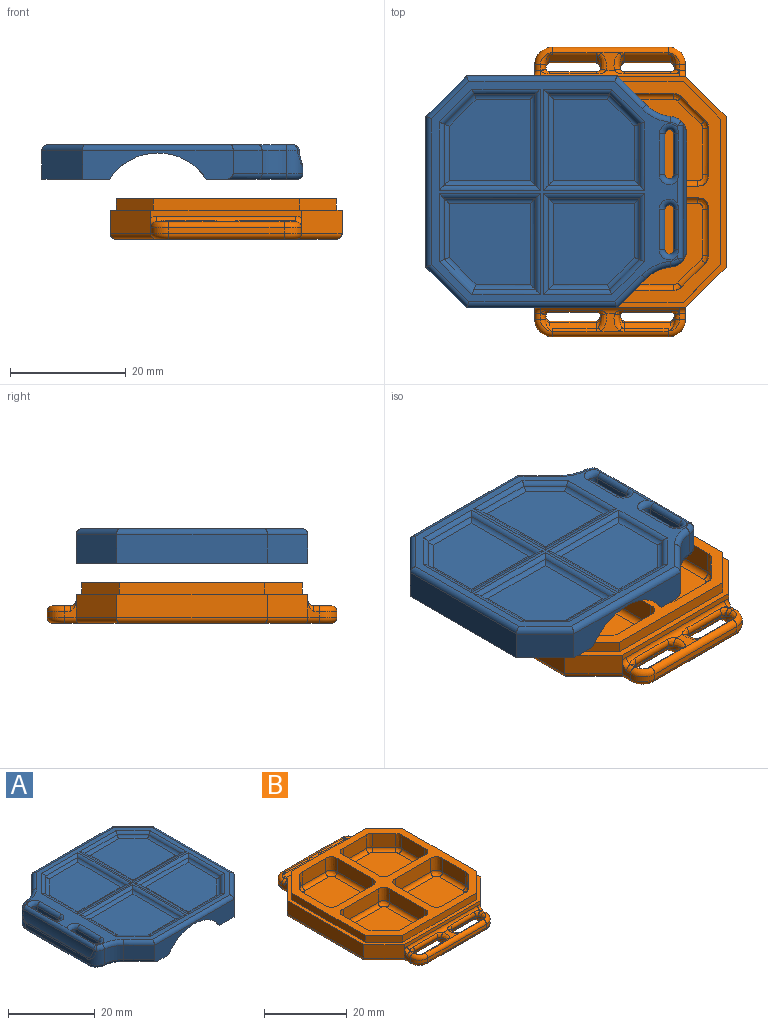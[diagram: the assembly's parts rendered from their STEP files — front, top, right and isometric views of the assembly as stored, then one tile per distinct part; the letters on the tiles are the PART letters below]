
ASSEMBLY  parts=2 mates=1
PART A: 123 faces, bbox 45.2x41.4x6 mm
  f0: plane 4.18x1mm, normal (0,0,-1), area 3.7mm2, adj f4,f22,f62,f69
  f1: plane 4.18x1mm, normal (0,0,-1), area 3.7mm2, adj f12,f17,f62,f63
  f2: plane 28.6x6.71mm, normal (0,0,-1), area 52.9mm2, adj f13,f14,f15,f64,f65,f66,f67,f68
  f3: plane 7.2x3mm, normal (0,1,0), area 16.4mm2, adj f6,f7,f11,f62
  f4: plane 26x5mm, normal (0,1,0), area 75.5mm2, adj f0,f7,f20,f21,f62,f69,f82
  f5: plane 7.2x3mm, normal (0,-1,0), area 16.4mm2, adj f6,f7,f9,f62
  f6: plane 38x13.61mm, normal (0,0,-1), area 476.1mm2, adj f3,f5,f9,f10,f11,f62
  f7: plane 40x11.6mm, normal (0,0,-1), area 53.3mm2, adj f3,f4,f5,f9,f10,f11,f17,f18
  f8: plane 42.38x38mm, normal (0,0,1), area 251.6mm2, adj f78,f79,f80,f81,f82,f83,f84,f85
  f9: plane 6.41x6.41mm, normal (-0.71,-0.71,0), area 27.2mm2, adj f5,f6,f7,f10
  f10: plane 25.17x3mm, normal (-1,0,0), area 75.5mm2, adj f6,f7,f9,f11
  f11: plane 6.41x6.41mm, normal (-0.71,0.71,0), area 27.2mm2, adj f3,f6,f7,f10
  f12: plane 7.2x3mm, normal (0,1,0), area 16.4mm2, adj f1,f13,f23,f62
  f13: plane 6.41x6.41mm, normal (0.71,0.71,0), area 27.2mm2, adj f2,f12,f14,f23,f63
  f14: plane 25.17x3mm, normal (1,0,0), area 75.5mm2, adj f2,f13,f15,f23
  f15: plane 6.41x6.41mm, normal (0.71,-0.71,0), area 27.2mm2, adj f2,f14,f22,f23,f69
  f16: plane 4.99x4.99mm, normal (-0.71,-0.71,0), area 28.3mm2, adj f17,f53,f63,f83
  f17: plane 26x5mm, normal (0,-1,0), area 75.5mm2, adj f1,f7,f16,f18,f62,f63,f81
  f18: plane 7x7mm, normal (0.71,-0.71,0), area 49.5mm2, adj f7,f17,f19,f79
  f19: plane 26x5mm, normal (1,0,0), area 130mm2, adj f7,f18,f20,f78
  f20: plane 7x7mm, normal (0.71,0.71,0), area 49.5mm2, adj f4,f7,f19,f80
  f21: plane 4.99x4.99mm, normal (-0.71,0.71,0), area 28.3mm2, adj f4,f52,f69,f84
  f22: plane 7.2x3mm, normal (0,-1,0), area 16.4mm2, adj f0,f15,f23,f62
  f23: plane 38x13.61mm, normal (0,0,-1), area 476.1mm2, adj f12,f13,f14,f15,f22,f62
  f24: plane 14x14mm, normal (0,0,1), area 185.2mm2, adj f43,f44,f45,f46,f47
  f25: plane 14x14mm, normal (0,0,1), area 185.2mm2, adj f38,f39,f40,f41,f42
  f26: plane 14x14mm, normal (0,0,1), area 185.2mm2, adj f28,f29,f30,f31,f32
  f27: plane 14x14mm, normal (0,0,1), area 185.2mm2, adj f33,f34,f35,f36,f37
  f28: cylinder r=1mm len=15.73mm, axis (0,-1,0), area 15.6mm2, adj f26,f29,f30,f122
  f29: cylinder r=1mm len=10.57mm, axis (-1,0,0), area 10.4mm2, adj f26,f28,f31,f121
  f30: cylinder r=1mm len=15.73mm, axis (1,0,0), area 15.6mm2, adj f26,f28,f32,f120
  f31: cylinder r=1mm len=5.78mm, axis (-0.71,0.71,0), area 7.3mm2, adj f26,f29,f32,f119
  f32: cylinder r=1mm len=10.57mm, axis (0,1,0), area 10.4mm2, adj f26,f30,f31,f118
  f33: cylinder r=1mm len=10.57mm, axis (0,-1,0), area 10.4mm2, adj f27,f34,f35,f114
  f34: cylinder r=1mm len=5.78mm, axis (-0.71,-0.71,0), area 7.3mm2, adj f27,f33,f36,f116
  f35: cylinder r=1mm len=15.73mm, axis (1,0,0), area 15.6mm2, adj f27,f33,f37,f113
  f36: cylinder r=1mm len=10.57mm, axis (-1,0,0), area 10.4mm2, adj f27,f34,f37,f117
  f37: cylinder r=1mm len=15.73mm, axis (0,1,0), area 15.6mm2, adj f27,f35,f36,f115
  f38: cylinder r=1mm len=5.78mm, axis (0.71,-0.71,0), area 7.3mm2, adj f25,f39,f40,f111
  f39: cylinder r=1mm len=10.57mm, axis (0,-1,0), area 10.4mm2, adj f25,f38,f41,f109
  f40: cylinder r=1mm len=10.57mm, axis (1,0,0), area 10.4mm2, adj f25,f38,f42,f112
  f41: cylinder r=1mm len=15.73mm, axis (-1,0,0), area 15.6mm2, adj f25,f39,f42,f108
  f42: cylinder r=1mm len=15.73mm, axis (0,1,0), area 15.6mm2, adj f25,f40,f41,f110
  f43: cylinder r=1mm len=15.73mm, axis (0,-1,0), area 15.6mm2, adj f24,f44,f45,f106
  f44: cylinder r=1mm len=15.73mm, axis (-1,0,0), area 15.6mm2, adj f24,f43,f46,f104
  f45: cylinder r=1mm len=10.57mm, axis (1,0,0), area 10.4mm2, adj f24,f43,f47,f107
  f46: cylinder r=1mm len=10.57mm, axis (0,1,0), area 10.4mm2, adj f24,f44,f47,f103
  f47: cylinder r=1mm len=5.78mm, axis (0.71,0.71,0), area 7.3mm2, adj f24,f45,f46,f105
  f48: plane 20x1.26mm, normal (-1,0,0), area 25.1mm2, adj f49,f50,f66,f86
  f49: cylinder r=3mm len=4mm, axis (0,0,1), area 12.8mm2, adj f48,f52,f67,f90,f91
  f50: cylinder r=3mm len=4mm, axis (0,0,-1), area 12.8mm2, adj f48,f53,f65,f88,f89
  f51: cylinder r=10mm len=22.9mm, axis (0,1,0), area 56.9mm2, adj f86,f89,f90,f100
  f52: cylinder r=7mm len=4.29mm, axis (0,0,1), area 19.3mm2, adj f21,f49,f68,f87
  f53: cylinder r=7mm len=4.29mm, axis (0,0,-1), area 19.3mm2, adj f16,f50,f64,f85
  f54: plane 7x4mm, normal (-1,0,0), area 28mm2, adj f55,f57,f70,f92
  f55: cylinder r=0.75mm len=4mm, axis (0,0,-1), area 9.4mm2, adj f54,f56,f72,f97
  f56: plane 7x4mm, normal (1,0,0), area 28mm2, adj f55,f57,f73,f96
  f57: cylinder r=0.75mm len=4mm, axis (0,0,-1), area 9.4mm2, adj f54,f56,f71,f95
  f58: cylinder r=0.75mm len=4mm, axis (0,0,-1), area 9.4mm2, adj f59,f61,f76,f102
  f59: plane 7x4mm, normal (-1,0,0), area 28mm2, adj f58,f60,f74,f101
  f60: cylinder r=0.75mm len=4mm, axis (0,0,-1), area 9.4mm2, adj f59,f61,f75,f98
  f61: plane 7x4mm, normal (1,0,0), area 28mm2, adj f58,f60,f77,f99
  f62: cylinder r=10mm len=40mm, axis (0,1,0), area 472.5mm2, adj f0,f1,f3,f4,f5,f6,f7,f12
  f63: cylinder r=1mm len=6.41mm, axis (-0.71,0.71,0), area 11.7mm2, adj f1,f13,f16,f17,f64
  f64: torus R=8mm, axis (0,0,1), area 8mm2, adj f2,f53,f63,f65
  f65: torus R=2mm, axis (0,0,1), area 6.1mm2, adj f2,f50,f64,f66
  f66: cylinder r=1mm len=20mm, axis (0,1,0), area 31.4mm2, adj f2,f48,f65,f67
  f67: torus R=2mm, axis (0,0,1), area 6.1mm2, adj f2,f49,f66,f68
  f68: torus R=8mm, axis (0,0,1), area 8mm2, adj f2,f52,f67,f69
  f69: cylinder r=1mm len=6.41mm, axis (0.71,0.71,0), area 11.7mm2, adj f0,f4,f15,f21,f68
  f70: cylinder r=1mm len=7mm, axis (0,-1,0), area 11mm2, adj f2,f54,f71,f72
  f71: torus R=1.75mm, axis (0,0,1), area 5.5mm2, adj f2,f57,f70,f73
  f72: torus R=1.75mm, axis (0,0,1), area 5.5mm2, adj f2,f55,f70,f73
  f73: cylinder r=1mm len=7mm, axis (0,1,0), area 11mm2, adj f2,f56,f71,f72
  f74: cylinder r=1mm len=7mm, axis (0,-1,0), area 11mm2, adj f2,f59,f75,f76
  f75: torus R=1.75mm, axis (0,0,1), area 5.5mm2, adj f2,f60,f74,f77
  f76: torus R=1.75mm, axis (0,0,1), area 5.5mm2, adj f2,f58,f74,f77
  f77: cylinder r=1mm len=7mm, axis (0,1,0), area 11mm2, adj f2,f61,f75,f76
  f78: cylinder r=1mm len=26mm, axis (0,1,0), area 40.2mm2, adj f8,f19,f79,f80
  f79: cylinder r=1mm len=7.71mm, axis (0.71,0.71,0), area 14.9mm2, adj f8,f18,f78,f81
  f80: cylinder r=1mm len=7.71mm, axis (-0.71,0.71,0), area 14.9mm2, adj f8,f20,f78,f82
  f81: cylinder r=1mm len=26mm, axis (1,0,0), area 40.2mm2, adj f8,f17,f79,f83
  f82: cylinder r=1mm len=26mm, axis (-1,0,0), area 40.2mm2, adj f4,f8,f80,f84
  f83: cylinder r=1mm len=5.7mm, axis (0.71,-0.71,0), area 10.8mm2, adj f8,f16,f81,f85
  f84: cylinder r=1mm len=5.7mm, axis (-0.71,-0.71,0), area 10.8mm2, adj f8,f21,f82,f87
  f85: torus R=8mm, axis (0,0,1), area 8mm2, adj f8,f53,f83,f88
  f86: cylinder r=1mm len=20mm, axis (0,1,0), area 7mm2, adj f48,f51,f89,f90
  f87: torus R=8mm, axis (0,0,1), area 8mm2, adj f8,f52,f84,f91
  f88: torus R=2mm, axis (0,0,1), area 2.8mm2, adj f8,f50,f85,f93
  f89: bspline ~3.06x2.45mm, area 2.1mm2, adj f50,f51,f86,f93
  f90: bspline ~3.06x2.45mm, area 2.1mm2, adj f49,f51,f86,f94
  f91: torus R=2mm, axis (0,0,1), area 2.8mm2, adj f8,f49,f87,f94
  f92: cylinder r=1mm len=7mm, axis (0,-1,0), area 11mm2, adj f8,f54,f95,f97
  f93: sphere r=1mm, area 0.8mm2, adj f88,f89,f100
  f94: sphere r=1mm, area 0.8mm2, adj f90,f91,f100
  f95: torus R=1.75mm, axis (0,0,1), area 5.4mm2, adj f8,f57,f92,f96,f100
  f96: cylinder r=1mm len=7mm, axis (0,1,0), area 9.7mm2, adj f56,f95,f97,f100
  f97: torus R=1.75mm, axis (0,0,1), area 5.4mm2, adj f8,f55,f92,f96,f100
  f98: torus R=1.75mm, axis (0,0,1), area 5.4mm2, adj f8,f60,f99,f100,f101
  f99: cylinder r=1mm len=7mm, axis (0,1,0), area 9.7mm2, adj f61,f98,f100,f102
  f100: cylinder r=1mm len=22.9mm, axis (0,1,0), area 30.8mm2, adj f8,f51,f93,f94,f95,f96,f97,f98
  f101: cylinder r=1mm len=7mm, axis (0,-1,0), area 11mm2, adj f8,f59,f98,f102
  f102: torus R=1.75mm, axis (0,0,1), area 5.4mm2, adj f8,f58,f99,f100,f101
  f103: cylinder r=1mm len=11.79mm, axis (0,1,0), area 11.7mm2, adj f8,f46,f104,f105
  f104: cylinder r=1mm len=17.46mm, axis (-1,0,0), area 17.4mm2, adj f8,f44,f103,f106
  f105: cylinder r=1mm len=6.28mm, axis (0.71,0.71,0), area 8mm2, adj f8,f47,f103,f107
  f106: cylinder r=1mm len=17.46mm, axis (0,-1,0), area 17.4mm2, adj f8,f43,f104,f107
  f107: cylinder r=1mm len=11.79mm, axis (1,0,0), area 11.7mm2, adj f8,f45,f105,f106
  f108: cylinder r=1mm len=17.46mm, axis (-1,0,0), area 17.4mm2, adj f8,f41,f109,f110
  f109: cylinder r=1mm len=11.79mm, axis (0,-1,0), area 11.7mm2, adj f8,f39,f108,f111
  f110: cylinder r=1mm len=17.46mm, axis (0,1,0), area 17.4mm2, adj f8,f42,f108,f112
  f111: cylinder r=1mm len=6.28mm, axis (0.71,-0.71,0), area 8mm2, adj f8,f38,f109,f112
  f112: cylinder r=1mm len=11.79mm, axis (1,0,0), area 11.7mm2, adj f8,f40,f110,f111
  f113: cylinder r=1mm len=17.46mm, axis (1,0,0), area 17.4mm2, adj f8,f35,f114,f115
  f114: cylinder r=1mm len=11.79mm, axis (0,-1,0), area 11.7mm2, adj f8,f33,f113,f116
  f115: cylinder r=1mm len=17.46mm, axis (0,1,0), area 17.4mm2, adj f8,f37,f113,f117
  f116: cylinder r=1mm len=6.28mm, axis (-0.71,-0.71,0), area 8mm2, adj f8,f34,f114,f117
  f117: cylinder r=1mm len=11.79mm, axis (-1,0,0), area 11.7mm2, adj f8,f36,f115,f116
  f118: cylinder r=1mm len=11.79mm, axis (0,1,0), area 11.7mm2, adj f8,f32,f119,f120
  f119: cylinder r=1mm len=6.28mm, axis (-0.71,0.71,0), area 8mm2, adj f8,f31,f118,f121
  f120: cylinder r=1mm len=17.46mm, axis (1,0,0), area 17.4mm2, adj f8,f30,f118,f122
  f121: cylinder r=1mm len=11.79mm, axis (-1,0,0), area 11.7mm2, adj f8,f29,f119,f122
  f122: cylinder r=1mm len=17.46mm, axis (0,-1,0), area 17.4mm2, adj f8,f28,f120,f121
PART B: 231 faces, bbox 40.2x50.7x7.6 mm
  f0: plane 9.05x0.34mm, normal (0,1,0), area 2.2mm2, adj f2,f193,f194,f196
  f1: plane 26x1.27mm, normal (0,1,0), area 26.2mm2, adj f38,f40,f44,f190,f191,f192
  f2: cylinder r=1mm len=10.39mm, axis (-1,0,0), area 15.2mm2, adj f0,f3,f194,f196,f202,f205
  f3: plane 48x38mm, normal (0,0,-1), area 1412.6mm2, adj f2,f112,f113,f114,f115,f116,f117,f118
  f4: plane 3.18x3mm, normal (0,0,1), area 5.2mm2, adj f127,f130,f153,f168
  f5: plane 38.21x38.21mm, normal (0,0,1), area 401.3mm2, adj f6,f7,f8,f9,f10,f12,f13,f14
  f6: plane 12x4mm, normal (-1,0,0), area 48mm2, adj f5,f50,f54,f75
  f7: plane 7.93x4mm, normal (0,-1,0), area 31.7mm2, adj f5,f54,f66,f71
  f8: plane 4.07x4.07mm, normal (0.71,-0.71,0), area 23mm2, adj f5,f65,f66,f67
  f9: plane 7.93x4mm, normal (1,0,0), area 31.7mm2, adj f5,f58,f65,f70
  f10: plane 12x4mm, normal (0,1,0), area 48mm2, adj f5,f50,f58,f74
  f11: plane 14x14mm, normal (0,0,1), area 184.8mm2, adj f67,f68,f69,f70,f71,f72,f73,f74
  f12: plane 7.93x4mm, normal (-1,0,0), area 31.7mm2, adj f5,f57,f62,f81
  f13: plane 4.07x4.07mm, normal (-0.71,-0.71,0), area 23mm2, adj f5,f62,f64,f77
  f14: plane 7.93x4mm, normal (0,-1,0), area 31.7mm2, adj f5,f53,f64,f80
  f15: plane 12x4mm, normal (1,0,0), area 48mm2, adj f5,f49,f53,f84
  f16: plane 12x4mm, normal (0,1,0), area 48mm2, adj f5,f49,f57,f85
  f17: plane 14x14mm, normal (0,0,1), area 184.8mm2, adj f77,f78,f79,f80,f81,f82,f83,f84
  f18: plane 12x4mm, normal (0,-1,0), area 48mm2, adj f5,f47,f55,f104
  f19: plane 12x4mm, normal (1,0,0), area 48mm2, adj f5,f47,f51,f105
  f20: plane 7.93x4mm, normal (0,1,0), area 31.7mm2, adj f5,f51,f60,f101
  f21: plane 4.07x4.07mm, normal (-0.71,0.71,0), area 23mm2, adj f5,f59,f60,f97
  f22: plane 7.93x4mm, normal (-1,0,0), area 31.7mm2, adj f5,f55,f59,f100
  f23: plane 14x14mm, normal (0,0,1), area 184.8mm2, adj f97,f98,f99,f100,f101,f102,f103,f104
  f24: plane 12x4mm, normal (-1,0,0), area 48mm2, adj f5,f48,f52,f94
  f25: plane 12x4mm, normal (0,-1,0), area 48mm2, adj f5,f48,f56,f95
  f26: plane 7.93x4mm, normal (1,0,0), area 31.7mm2, adj f5,f56,f63,f91
  f27: plane 4.07x4.07mm, normal (0.71,0.71,0), area 23mm2, adj f5,f61,f63,f87
  f28: plane 7.93x4mm, normal (0,1,0), area 31.7mm2, adj f5,f52,f61,f90
  f29: plane 14x14mm, normal (0,0,1), area 184.8mm2, adj f87,f88,f89,f90,f91,f92,f93,f94
  f30: plane 6.41x6.41mm, normal (0.71,0.71,0), area 18.1mm2, adj f5,f31,f37,f38
  f31: plane 25.17x2mm, normal (1,0,0), area 50.3mm2, adj f5,f30,f32,f38
  f32: plane 6.41x6.41mm, normal (0.71,-0.71,0), area 18.1mm2, adj f5,f31,f33,f38
  f33: plane 25.17x2mm, normal (0,-1,0), area 50.3mm2, adj f5,f32,f34,f38
  f34: plane 6.41x6.41mm, normal (-0.71,-0.71,0), area 18.1mm2, adj f5,f33,f35,f38
  f35: plane 25.17x2mm, normal (-1,0,0), area 50.3mm2, adj f5,f34,f36,f38
  f36: plane 6.41x6.41mm, normal (-0.71,0.71,0), area 18.1mm2, adj f5,f35,f37,f38
  f37: plane 25.17x2mm, normal (0,1,0), area 50.3mm2, adj f5,f30,f36,f38
  f38: plane 40x40mm, normal (0,0,1), area 140.3mm2, adj f1,f30,f31,f32,f33,f34,f35,f36
  f39: plane 7x7mm, normal (0.71,-0.71,0), area 39.6mm2, adj f38,f41,f43,f108,f115
  f40: plane 7x7mm, normal (0.71,0.71,0), area 39.6mm2, adj f1,f38,f41,f112,f176
  f41: plane 26x4mm, normal (1,0,0), area 104mm2, adj f38,f39,f40,f113
  f42: plane 7x7mm, normal (-0.71,-0.71,0), area 39.6mm2, adj f38,f43,f45,f107,f120
  f43: plane 26x1.27mm, normal (0,-1,0), area 26.2mm2, adj f38,f39,f42,f129,f130,f131
  f44: plane 7x7mm, normal (-0.71,0.71,0), area 39.6mm2, adj f1,f38,f45,f116,f175
  f45: plane 26x4mm, normal (-1,0,0), area 104mm2, adj f38,f42,f44,f118
  f46: plane 9.05x0.34mm, normal (0,1,0), area 2.2mm2, adj f114,f197,f199,f200
  f47: bspline ~5.5x2mm, area 13mm2, adj f5,f18,f19,f106
  f48: bspline ~5.5x2mm, area 13mm2, adj f5,f24,f25,f96
  f49: bspline ~5.5x2mm, area 13mm2, adj f5,f15,f16,f86
  f50: bspline ~5.5x2mm, area 13mm2, adj f5,f6,f10,f76
  f51: bspline ~5.5x2mm, area 13mm2, adj f5,f19,f20,f103
  f52: bspline ~5.5x2mm, area 13mm2, adj f5,f24,f28,f92
  f53: bspline ~5.5x2mm, area 13mm2, adj f5,f14,f15,f82
  f54: bspline ~5.5x2mm, area 13mm2, adj f5,f6,f7,f73
  f55: bspline ~5.5x2mm, area 13mm2, adj f5,f18,f22,f102
  f56: bspline ~5.5x2mm, area 13mm2, adj f5,f25,f26,f93
  f57: bspline ~5.5x2mm, area 13mm2, adj f5,f12,f16,f83
  f58: bspline ~5.5x2mm, area 13mm2, adj f5,f9,f10,f72
  f59: bspline ~5.5x1.41mm, area 6.3mm2, adj f5,f21,f22,f98
  f60: bspline ~5.5x1.41mm, area 6.3mm2, adj f5,f20,f21,f99
  f61: bspline ~5.5x1.41mm, area 6.3mm2, adj f5,f27,f28,f88
  f62: bspline ~5.5x1.41mm, area 6.3mm2, adj f5,f12,f13,f79
  f63: bspline ~5.5x1.41mm, area 6.3mm2, adj f5,f26,f27,f89
  f64: bspline ~5.5x1.41mm, area 6.3mm2, adj f5,f13,f14,f78
  f65: bspline ~5.5x1.41mm, area 6.3mm2, adj f5,f8,f9,f68
  f66: bspline ~5.5x1.41mm, area 6.3mm2, adj f5,f7,f8,f69
  f67: cylinder r=1mm len=4.78mm, axis (-0.71,-0.71,0), area 9mm2, adj f8,f11,f68,f69
  f68: bspline ~1.65x1.46mm, area 2mm2, adj f11,f65,f67,f70
  f69: bspline ~1.7x1.34mm, area 2mm2, adj f11,f66,f67,f71
  f70: cylinder r=1mm len=7.93mm, axis (0,-1,0), area 12.5mm2, adj f9,f11,f68,f72
  f71: cylinder r=1mm len=7.93mm, axis (-1,0,0), area 12.5mm2, adj f7,f11,f69,f73
  f72: bspline ~2.52x2.52mm, area 4.2mm2, adj f11,f58,f70,f74
  f73: bspline ~2.52x2.52mm, area 4.2mm2, adj f11,f54,f71,f75
  f74: cylinder r=1mm len=12mm, axis (1,0,0), area 18.8mm2, adj f10,f11,f72,f76
  f75: cylinder r=1mm len=12mm, axis (0,1,0), area 18.8mm2, adj f6,f11,f73,f76
  f76: bspline ~2.52x2.52mm, area 4.2mm2, adj f11,f50,f74,f75
  f77: cylinder r=1mm len=4.78mm, axis (-0.71,0.71,0), area 9mm2, adj f13,f17,f78,f79
  f78: bspline ~1.65x1.46mm, area 2mm2, adj f17,f64,f77,f80
  f79: bspline ~1.7x1.34mm, area 2mm2, adj f17,f62,f77,f81
  f80: cylinder r=1mm len=7.93mm, axis (-1,0,0), area 12.5mm2, adj f14,f17,f78,f82
  f81: cylinder r=1mm len=7.93mm, axis (0,1,0), area 12.5mm2, adj f12,f17,f79,f83
  f82: bspline ~2.52x2.52mm, area 4.2mm2, adj f17,f53,f80,f84
  f83: bspline ~2.52x2.52mm, area 4.2mm2, adj f17,f57,f81,f85
  f84: cylinder r=1mm len=12mm, axis (0,-1,0), area 18.8mm2, adj f15,f17,f82,f86
  f85: cylinder r=1mm len=12mm, axis (1,0,0), area 18.8mm2, adj f16,f17,f83,f86
  f86: bspline ~2.52x2.52mm, area 4.2mm2, adj f17,f49,f84,f85
  f87: cylinder r=1mm len=4.78mm, axis (0.71,-0.71,0), area 9mm2, adj f27,f29,f88,f89
  f88: bspline ~1.65x1.46mm, area 2mm2, adj f29,f61,f87,f90
  f89: bspline ~1.7x1.34mm, area 2mm2, adj f29,f63,f87,f91
  f90: cylinder r=1mm len=7.93mm, axis (1,0,0), area 12.5mm2, adj f28,f29,f88,f92
  f91: cylinder r=1mm len=7.93mm, axis (0,-1,0), area 12.5mm2, adj f26,f29,f89,f93
  f92: bspline ~2.52x2.52mm, area 4.2mm2, adj f29,f52,f90,f94
  f93: bspline ~2.52x2.52mm, area 4.2mm2, adj f29,f56,f91,f95
  f94: cylinder r=1mm len=12mm, axis (0,1,0), area 18.8mm2, adj f24,f29,f92,f96
  f95: cylinder r=1mm len=12mm, axis (-1,0,0), area 18.8mm2, adj f25,f29,f93,f96
  f96: bspline ~2.52x2.52mm, area 4.2mm2, adj f29,f48,f94,f95
  f97: cylinder r=1mm len=4.78mm, axis (0.71,0.71,0), area 9mm2, adj f21,f23,f98,f99
  f98: bspline ~1.65x1.46mm, area 2mm2, adj f23,f59,f97,f100
  f99: bspline ~1.7x1.34mm, area 2mm2, adj f23,f60,f97,f101
  f100: cylinder r=1mm len=7.93mm, axis (0,1,0), area 12.5mm2, adj f22,f23,f98,f102
  f101: cylinder r=1mm len=7.93mm, axis (1,0,0), area 12.5mm2, adj f20,f23,f99,f103
  f102: bspline ~2.52x2.52mm, area 4.2mm2, adj f23,f55,f100,f104
  f103: bspline ~2.52x2.52mm, area 4.2mm2, adj f23,f51,f101,f105
  f104: cylinder r=1mm len=12mm, axis (-1,0,0), area 18.8mm2, adj f18,f23,f102,f106
  f105: cylinder r=1mm len=12mm, axis (0,-1,0), area 18.8mm2, adj f19,f23,f103,f106
  f106: bspline ~2.52x2.52mm, area 4.2mm2, adj f23,f47,f104,f105
  f107: plane 2.73x2mm, normal (-1,0,0), area 2.6mm2, adj f42,f110,f122,f126,f131
  f108: plane 2.73x2mm, normal (1,0,0), area 2.6mm2, adj f39,f111,f117,f124,f129
  f109: plane 20x1mm, normal (0,-1,0), area 20mm2, adj f110,f111,f121,f127
  f110: cylinder r=3mm len=3mm, axis (0,0,1), area 4.7mm2, adj f107,f109,f123,f128
  f111: cylinder r=3mm len=3mm, axis (0,0,-1), area 4.7mm2, adj f108,f109,f119,f125
  f112: cylinder r=1mm len=8mm, axis (0.71,-0.71,0), area 15.6mm2, adj f3,f40,f113,f180
  f113: cylinder r=1mm len=26mm, axis (0,1,0), area 40.2mm2, adj f3,f41,f112,f115
  f114: cylinder r=1mm len=10.39mm, axis (-1,0,0), area 15.2mm2, adj f3,f46,f197,f199,f216,f217
  f115: cylinder r=1mm len=8mm, axis (0.71,0.71,0), area 15.6mm2, adj f3,f39,f113,f117
  f116: cylinder r=1mm len=8mm, axis (-0.71,-0.71,0), area 15.6mm2, adj f3,f44,f118,f183
  f117: cylinder r=1mm len=2.41mm, axis (0,1,0), area 3.4mm2, adj f3,f108,f115,f119,f140
  f118: cylinder r=1mm len=26mm, axis (0,-1,0), area 40.2mm2, adj f3,f45,f116,f120
  f119: torus R=2mm, axis (0,0,1), area 6.5mm2, adj f3,f111,f117,f121
  f120: cylinder r=1mm len=8mm, axis (-0.71,0.71,0), area 15.6mm2, adj f3,f42,f118,f122
  f121: cylinder r=1mm len=20mm, axis (-1,0,0), area 31.4mm2, adj f3,f109,f119,f123
  f122: cylinder r=1mm len=2.41mm, axis (0,1,0), area 3.4mm2, adj f3,f107,f120,f123,f158
  f123: torus R=2mm, axis (0,0,1), area 6.5mm2, adj f3,f110,f121,f122
  f124: cylinder r=1mm len=1mm, axis (0,-1,0), area 1.6mm2, adj f108,f125,f129,f146
  f125: torus R=2mm, axis (0,0,1), area 6.5mm2, adj f111,f124,f127,f145,f147
  f126: cylinder r=1mm len=1mm, axis (0,-1,0), area 1.6mm2, adj f107,f128,f131,f161
  f127: cylinder r=1mm len=20mm, axis (1,0,0), area 31.4mm2, adj f4,f109,f125,f128,f149,f151,f164,f166
  f128: torus R=2mm, axis (0,0,1), area 6.5mm2, adj f110,f126,f127,f160,f162
  f129: torus R=2mm, axis (0,1,0), area 1.9mm2, adj f43,f108,f124,f130,f148
  f130: cylinder r=1mm len=24mm, axis (1,0,0), area 24.7mm2, adj f4,f43,f129,f131,f150,f152,f154,f165
  f131: torus R=2mm, axis (0,1,0), area 1.9mm2, adj f43,f107,f126,f130,f163
  f132: plane 8x0.47mm, normal (0,-0.71,-0.71), area 5.3mm2, adj f133,f135,f152,f173
  f133: cylinder r=0.75mm len=3.97mm, axis (0,-0.71,0.71), area 2.8mm2, adj f132,f134,f144,f151,f153,f154,f172,f173
  f134: plane 8x1.09mm, normal (0,0.71,0.71), area 12mm2, adj f133,f135,f143,f147,f149
  f135: cylinder r=0.75mm len=4.01mm, axis (0,-0.71,0.71), area 3mm2, adj f132,f134,f140,f141,f142,f145,f146,f148
  f136: cylinder r=0.75mm len=4.01mm, axis (0,-0.71,0.71), area 3mm2, adj f137,f139,f156,f158,f159,f160,f161,f163
  f137: plane 8x1.09mm, normal (0,0.71,0.71), area 12mm2, adj f136,f138,f157,f162,f164
  f138: cylinder r=0.75mm len=3.97mm, axis (0,-0.71,0.71), area 2.8mm2, adj f137,f139,f155,f166,f168,f169,f170,f171
  f139: plane 8x0.47mm, normal (0,-0.71,-0.71), area 5.3mm2, adj f136,f138,f167,f171
  f140: bspline ~2.57x1.43mm, area 2.4mm2, adj f117,f135,f141,f142
  f141: bspline ~1.08x1.08mm, area 0.6mm2, adj f3,f135,f140,f172
  f142: bspline ~2.41x2.1mm, area 3mm2, adj f3,f135,f140,f143
  f143: cylinder r=1mm len=8mm, axis (1,0,0), area 18.8mm2, adj f3,f134,f142,f144
  f144: bspline ~4.5x2.2mm, area 6.2mm2, adj f3,f133,f143,f172
  f145: bspline ~2.02x1.66mm, area 1.9mm2, adj f125,f135,f146,f147
  f146: bspline ~1.58x1.28mm, area 1.3mm2, adj f124,f135,f145,f148
  f147: bspline ~0.64x0.36mm, area 0.2mm2, adj f125,f134,f145,f149
  f148: bspline ~1.29x0.94mm, area 0.2mm2, adj f129,f135,f146,f150
  f149: cylinder r=1mm len=7.59mm, axis (1,0,0), area 3.3mm2, adj f127,f134,f147,f151
  f150: bspline ~2.04x1.56mm, area 1.8mm2, adj f130,f135,f148,f152
  f151: bspline ~1.07x0.74mm, area 0.4mm2, adj f127,f133,f149,f153
  f152: cylinder r=1mm len=8mm, axis (1,0,0), area 13.5mm2, adj f130,f132,f150,f154
  f153: bspline ~3x1.4mm, area 3.5mm2, adj f4,f133,f151,f154
  f154: bspline ~2.06x1.56mm, area 2mm2, adj f130,f133,f152,f153
  f155: bspline ~4.5x2.2mm, area 6.2mm2, adj f3,f138,f157,f170
  f156: bspline ~1.08x1.08mm, area 0.6mm2, adj f3,f136,f158,f170
  f157: cylinder r=1mm len=8mm, axis (1,0,0), area 18.8mm2, adj f3,f137,f155,f159
  f158: bspline ~2.57x1.43mm, area 2.4mm2, adj f122,f136,f156,f159
  f159: bspline ~2.41x2.1mm, area 3mm2, adj f3,f136,f157,f158
  f160: bspline ~2.02x1.66mm, area 1.9mm2, adj f128,f136,f161,f162
  f161: bspline ~1.58x1.28mm, area 1.3mm2, adj f126,f136,f160,f163
  f162: bspline ~0.74x0.36mm, area 0.2mm2, adj f128,f137,f160,f164
  f163: bspline ~1.29x0.94mm, area 0.2mm2, adj f131,f136,f161,f165
  f164: cylinder r=1mm len=7.59mm, axis (1,0,0), area 3.3mm2, adj f127,f137,f162,f166
  f165: bspline ~2.04x1.56mm, area 1.8mm2, adj f130,f136,f163,f167
  f166: bspline ~1.07x0.74mm, area 0.4mm2, adj f127,f138,f164,f168
  f167: cylinder r=1mm len=8mm, axis (1,0,0), area 13.5mm2, adj f130,f139,f165,f169
  f168: bspline ~3x1.4mm, area 3.5mm2, adj f4,f138,f166,f169
  f169: bspline ~1.82x1.56mm, area 2mm2, adj f130,f138,f167,f168
  f170: cylinder r=1mm len=10.39mm, axis (-1,0,0), area 15.2mm2, adj f3,f136,f138,f155,f156,f171
  f171: plane 9.05x0.34mm, normal (0,-1,0), area 2.2mm2, adj f136,f138,f139,f170
  f172: cylinder r=1mm len=10.39mm, axis (-1,0,0), area 15.2mm2, adj f3,f133,f135,f141,f144,f173
  f173: plane 9.05x0.34mm, normal (0,-1,0), area 2.2mm2, adj f132,f133,f135,f172
  f174: plane 3.18x3mm, normal (0,0,1), area 5.2mm2, adj f188,f191,f214,f229
  f175: plane 2.73x2mm, normal (-1,0,0), area 2.6mm2, adj f44,f178,f183,f187,f192
  f176: plane 2.73x2mm, normal (1,0,0), area 2.6mm2, adj f40,f179,f180,f185,f190
  f177: plane 20x1mm, normal (0,1,0), area 20mm2, adj f178,f179,f182,f188
  f178: cylinder r=3mm len=3mm, axis (0,0,1), area 4.7mm2, adj f175,f177,f184,f189
  f179: cylinder r=3mm len=3mm, axis (0,0,-1), area 4.7mm2, adj f176,f177,f181,f186
  f180: cylinder r=1mm len=2.41mm, axis (0,-1,0), area 3.4mm2, adj f3,f112,f176,f181,f201
  f181: torus R=2mm, axis (0,0,1), area 6.5mm2, adj f3,f179,f180,f182
  f182: cylinder r=1mm len=20mm, axis (-1,0,0), area 31.4mm2, adj f3,f177,f181,f184
  f183: cylinder r=1mm len=2.41mm, axis (0,-1,0), area 3.4mm2, adj f3,f116,f175,f184,f219
  f184: torus R=2mm, axis (0,0,1), area 6.5mm2, adj f3,f178,f182,f183
  f185: cylinder r=1mm len=1mm, axis (0,1,0), area 1.6mm2, adj f176,f186,f190,f207
  f186: torus R=2mm, axis (0,0,1), area 6.5mm2, adj f179,f185,f188,f206,f208
  f187: cylinder r=1mm len=1mm, axis (0,1,0), area 1.6mm2, adj f175,f189,f192,f222
  f188: cylinder r=1mm len=20mm, axis (1,0,0), area 31.4mm2, adj f174,f177,f186,f189,f210,f212,f225,f227
  f189: torus R=2mm, axis (0,0,1), area 6.5mm2, adj f178,f187,f188,f221,f223
  f190: torus R=2mm, axis (0,-1,0), area 1.9mm2, adj f1,f176,f185,f191,f209
  f191: cylinder r=1mm len=24mm, axis (1,0,0), area 24.7mm2, adj f1,f174,f190,f192,f211,f213,f215,f226
  f192: torus R=2mm, axis (0,-1,0), area 1.9mm2, adj f1,f175,f187,f191,f224
  f193: plane 8x0.47mm, normal (0,0.71,-0.71), area 5.3mm2, adj f0,f194,f196,f213
  f194: cylinder r=0.75mm len=3.97mm, axis (0,0.71,0.71), area 2.8mm2, adj f0,f2,f193,f195,f205,f212,f214,f215
  f195: plane 8x1.09mm, normal (0,-0.71,0.71), area 12mm2, adj f194,f196,f204,f208,f210
  f196: cylinder r=0.75mm len=4.01mm, axis (0,0.71,0.71), area 3mm2, adj f0,f2,f193,f195,f201,f202,f203,f206
  f197: cylinder r=0.75mm len=4.01mm, axis (0,0.71,0.71), area 3mm2, adj f46,f114,f198,f200,f217,f219,f220,f221
  f198: plane 8x1.09mm, normal (0,-0.71,0.71), area 12mm2, adj f197,f199,f218,f223,f225
  f199: cylinder r=0.75mm len=3.97mm, axis (0,0.71,0.71), area 2.8mm2, adj f46,f114,f198,f200,f216,f227,f229,f230
  f200: plane 8x0.47mm, normal (0,0.71,-0.71), area 5.3mm2, adj f46,f197,f199,f228
  f201: bspline ~2.57x1.43mm, area 2.4mm2, adj f180,f196,f202,f203
  f202: bspline ~1.08x1.08mm, area 0.6mm2, adj f2,f3,f196,f201
  f203: bspline ~2.41x2.1mm, area 3mm2, adj f3,f196,f201,f204
  f204: cylinder r=1mm len=8mm, axis (1,0,0), area 18.8mm2, adj f3,f195,f203,f205
  f205: bspline ~4.5x2.2mm, area 6.2mm2, adj f2,f3,f194,f204
  f206: bspline ~2.02x1.66mm, area 1.9mm2, adj f186,f196,f207,f208
  f207: bspline ~1.58x1.28mm, area 1.3mm2, adj f185,f196,f206,f209
  f208: bspline ~0.64x0.36mm, area 0.2mm2, adj f186,f195,f206,f210
  f209: bspline ~1.32x1.26mm, area 0.2mm2, adj f190,f196,f207,f211
  f210: cylinder r=1mm len=7.59mm, axis (1,0,0), area 3.3mm2, adj f188,f195,f208,f212
  f211: bspline ~2.04x1.56mm, area 1.8mm2, adj f191,f196,f209,f213
  f212: bspline ~1.07x0.74mm, area 0.4mm2, adj f188,f194,f210,f214
  f213: cylinder r=1mm len=8mm, axis (1,0,0), area 13.5mm2, adj f191,f193,f211,f215
  f214: bspline ~3x1.4mm, area 3.5mm2, adj f174,f194,f212,f215
  f215: bspline ~2.06x1.56mm, area 2mm2, adj f191,f194,f213,f214
  f216: bspline ~4.5x2.2mm, area 6.2mm2, adj f3,f114,f199,f218
  f217: bspline ~1.08x1.08mm, area 0.6mm2, adj f3,f114,f197,f219
  f218: cylinder r=1mm len=8mm, axis (1,0,0), area 18.8mm2, adj f3,f198,f216,f220
  f219: bspline ~2.57x1.43mm, area 2.4mm2, adj f183,f197,f217,f220
  f220: bspline ~2.41x2.1mm, area 3mm2, adj f3,f197,f218,f219
  f221: bspline ~2.02x1.66mm, area 1.9mm2, adj f189,f197,f222,f223
  f222: bspline ~1.58x1.28mm, area 1.3mm2, adj f187,f197,f221,f224
  f223: bspline ~0.74x0.36mm, area 0.2mm2, adj f189,f198,f221,f225
  f224: bspline ~1.32x1.27mm, area 0.2mm2, adj f192,f197,f222,f226
  f225: cylinder r=1mm len=7.59mm, axis (1,0,0), area 3.3mm2, adj f188,f198,f223,f227
  f226: bspline ~2.04x1.56mm, area 1.8mm2, adj f191,f197,f224,f228
  f227: bspline ~1.07x0.74mm, area 0.4mm2, adj f188,f199,f225,f229
  f228: cylinder r=1mm len=8mm, axis (1,0,0), area 13.5mm2, adj f191,f200,f226,f230
  f229: bspline ~3x1.4mm, area 3.5mm2, adj f174,f199,f227,f230
  f230: bspline ~2.1x1.56mm, area 2mm2, adj f191,f199,f228,f229
PLACE A rot(axis=(0,0,-1),180deg) t=(-42.79,3.17,18.64)mm
PLACE B rot(axis=(0,0,-1),180deg) t=(-31,3.17,12.32)mm
MATE slider A.f23 <-> B.f5  axis (0,0,-1) through (-31,3.17,25.64)mm
